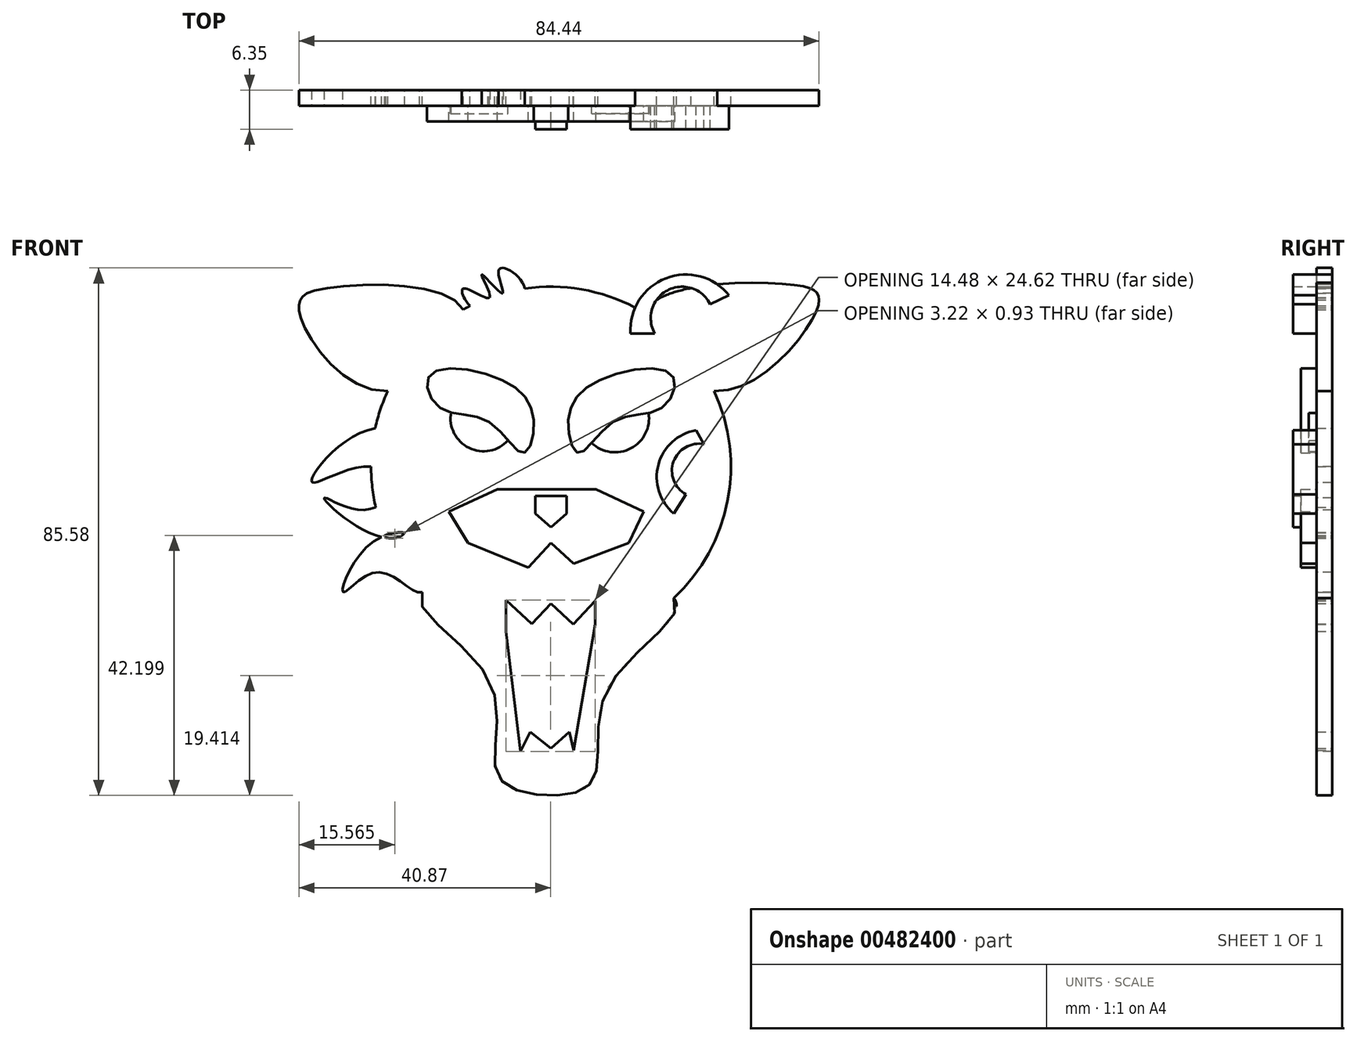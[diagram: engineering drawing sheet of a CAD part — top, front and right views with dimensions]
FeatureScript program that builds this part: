
annotation { "Feature Type Name" : "Feature", "Feature Type Description" : "" }
export const myFeature = defineFeature(function(context is Context, id is Id, definition is map)
    precondition{}
    {
        {
            var Q0;
            Q0=qCreatedBy(makeId("Front.planeOp"),FACE);
            var sketch = newSketch(context, id + "F0", { "sketchPlane" : qUnion([Q0])});
            skCircle(sketch, "E0", {"center": v(0, 0) * mm, "radius": 29.2 * mm});
            skFitSpline(sketch, "E1", {"points": [v(-20.92, -20.37) * mm, v(-10.1, -34.53) * mm, v(-8.7, -49.97) * mm, v(0, -53.34) * mm, v(7.02, -50.53) * mm, v(9.55, -35.37) * mm, v(19.93, -21.34) * mm, v(-20.92, -20.37) * mm]});
            skFitSpline(sketch, "E2", {"points": [v(-26.5, 12.27) * mm, v(-40.43, 23.58) * mm, v(-40.7, 26.95) * mm, v(-38.18, 28.64) * mm, v(-14.22, 25.5) * mm, v(-26.5, 12.27) * mm]});
            skFitSpline(sketch, "E3", {"points": [v(26.5, 12.27) * mm, v(42.95, 24.99) * mm, v(43.23, 28.07) * mm, v(39.58, 29.48) * mm, v(15.1, 25) * mm, v(26.5, 12.27) * mm]});
            skFitSpline(sketch, "E4", {"points": [v(-20.92, -20.37) * mm, v(-28.07, -17.12) * mm, v(-33.69, -20.37) * mm, v(-29.76, -12.91) * mm, v(-20.92, -12.35) * mm, v(-20.92, -20.37) * mm]});
            skFitSpline(sketch, "E5", {"points": [v(-23.75, -10.72) * mm, v(-31.72, -9.55) * mm, v(-36.78, -5.05) * mm, v(-30.6, -7.02) * mm, v(-24.14, -5.61) * mm, v(-23.75, -10.72) * mm]});
            skFitSpline(sketch, "E6", {"points": [v(-20.92, -3.09) * mm, v(-29.2, 0) * mm, v(-38.74, -2.53) * mm, v(-32.28, 4.77) * mm, v(-20.92, 4.21) * mm, v(-20.92, -3.09) * mm]});
            skFitSpline(sketch, "E7", {"points": [v(-10.67, 24.42) * mm, v(-14.22, 28.92) * mm, v(-9.96, 27.45) * mm, v(-11.23, 31.16) * mm, v(-7.86, 28.12) * mm, v(-8.42, 32) * mm, v(-4.24, 28.89) * mm, v(-10.67, 24.42) * mm]});
            skSolve(sketch);
        }
        {
            var Q0;
            Q0 = qSketchRegion(id + "F0", true);
            extrude(context, id + "F1", {"entities" : qUnion([Q0]), "depth" : 2.54 * mm});
        }
        {
            var Q0;
            Q0=qCreatedBy(makeId("Front.planeOp"),FACE);
            var sketch = newSketch(context, id + "F2", { "sketchPlane" : qUnion([Q0])});
            skFitSpline(sketch, "E8", {"points": [v(-17.97, 9.55) * mm, v(-10.1, 7.3) * mm, v(-4.5, 2.25) * mm, v(-2.8, 7.58) * mm, v(-7.86, 14.04) * mm, v(-19.65, 14.88) * mm, v(-17.97, 9.55) * mm]});
            skLineSegment(sketch, "E9", {"start": v(-8.7, -3.65) * mm, "end": v(0, -3.65) * mm});
            skLineSegment(sketch, "E10", {"start": v(0, -3.65) * mm, "end": v(7.3, -3.65) * mm});
            skLineSegment(sketch, "E11", {"start": v(7.3, -3.65) * mm, "end": v(15.02, -7.3) * mm});
            skLineSegment(sketch, "E12", {"start": v(15.02, -7.3) * mm, "end": v(12.63, -12.35) * mm});
            skLineSegment(sketch, "E13", {"start": v(12.63, -12.35) * mm, "end": v(3.65, -15.72) * mm});
            skLineSegment(sketch, "E14", {"start": v(3.65, -15.72) * mm, "end": v(0, -12.35) * mm});
            skLineSegment(sketch, "E15", {"start": v(0, -12.35) * mm, "end": v(-3.68, -16.34) * mm});
            skLineSegment(sketch, "E16", {"start": v(-3.68, -16.34) * mm, "end": v(-13.48, -12.35) * mm});
            skLineSegment(sketch, "E17", {"start": v(-13.48, -12.35) * mm, "end": v(-16.56, -7.3) * mm});
            skLineSegment(sketch, "E18", {"start": v(-16.56, -7.3) * mm, "end": v(-8.7, -3.65) * mm});
            skFitSpline(sketch, "E19.MirrorC", {"points": [v(17.97, 9.55) * mm, v(10.1, 7.3) * mm, v(4.5, 2.25) * mm, v(2.8, 7.58) * mm, v(7.86, 14.04) * mm, v(19.65, 14.88) * mm, v(17.97, 9.55) * mm]});
            skSolve(sketch);
        }
        {
            var Q0;
            Q0 = qSketchRegion(id + "F2", true);
            extrude(context, id + "F3", {"entities" : qUnion([Q0]), "operationType" : NewBodyOperationType.ADD, "depth" : 5.08 * mm});
        }
        {
            var Q0;
            Q0=qCreatedBy(makeId("Front.planeOp"),FACE);
            var sketch = newSketch(context, id + "F4", { "sketchPlane" : qUnion([Q0])});
            skLineSegment(sketch, "E20", {"start": v(-7.3, -26.7) * mm, "end": v(-7.3, -21.62) * mm});
            skLineSegment(sketch, "E21", {"start": v(-7.3, -21.62) * mm, "end": v(-3.09, -25.55) * mm});
            skLineSegment(sketch, "E22", {"start": v(-3.09, -25.55) * mm, "end": v(0, -22.24) * mm});
            skLineSegment(sketch, "E23", {"start": v(0, -22.24) * mm, "end": v(3.6, -25.6) * mm});
            skLineSegment(sketch, "E24", {"start": v(3.6, -25.6) * mm, "end": v(7.18, -21.77) * mm});
            skLineSegment(sketch, "E25", {"start": v(7.18, -21.77) * mm, "end": v(7.18, -25.6) * mm});
            skLineSegment(sketch, "E26", {"start": v(7.18, -25.6) * mm, "end": v(3.6, -46.6) * mm});
            skLineSegment(sketch, "E27", {"start": v(-4.93, -46.6) * mm, "end": v(-7.3, -26.7) * mm});
            skLineSegment(sketch, "E28", {"start": v(3.6, -46.6) * mm, "end": v(-4.93, -46.6) * mm});
            skSolve(sketch);
        }
        {
            var Q0;
            Q0 = qSketchRegion(id + "F4", true);
            extrude(context, id + "F5", {"entities" : qUnion([Q0]), "operationType" : NewBodyOperationType.REMOVE, "oppositeDirection" : true, "depth" : -2.54 * mm});
        }
        {
            var Q0;
            Q0=qCreatedBy(makeId("Front.planeOp"),FACE);
            var sketch = newSketch(context, id + "F6", { "sketchPlane" : qUnion([Q0])});
            skCircle(sketch, "E29", {"center": v(-10.95, 7.86) * mm, "radius": 5.36 * mm});
            skCircle(sketch, "E30", {"center": v(10.39, 7.86) * mm, "radius": 5.53 * mm});
            skSolve(sketch);
        }
        {
            var Q0;
            Q0 = qSketchRegion(id + "F6", true);
            extrude(context, id + "F7", {"entities" : qUnion([Q0]), "operationType" : NewBodyOperationType.ADD, "depth" : 3.8 * mm});
        }
        {
            var Q0;
            Q0=qCreatedBy(makeId("Front.planeOp"),FACE);
            var sketch = newSketch(context, id + "F8", { "sketchPlane" : qUnion([Q0])});
            skLineSegment(sketch, "E31", {"start": v(0, -9.83) * mm, "end": v(-2.53, -7.58) * mm});
            skLineSegment(sketch, "E32", {"start": v(-2.53, -7.58) * mm, "end": v(-2.53, -4.77) * mm});
            skLineSegment(sketch, "E33", {"start": v(-2.53, -4.77) * mm, "end": v(2.53, -4.77) * mm});
            skLineSegment(sketch, "E34", {"start": v(2.53, -4.77) * mm, "end": v(2.53, -7.58) * mm});
            skLineSegment(sketch, "E35", {"start": v(2.53, -7.58) * mm, "end": v(0, -9.83) * mm});
            skSolve(sketch);
        }
        {
            var Q0;
            Q0 = qSketchRegion(id + "F8", true);
            extrude(context, id + "F9", {"entities" : qUnion([Q0]), "operationType" : NewBodyOperationType.ADD, "depth" : 6.35 * mm});
        }
        {
            var Q0;
            Q0=qCreatedBy(makeId("Front.planeOp"),FACE);
            var sketch = newSketch(context, id + "F10", { "sketchPlane" : qUnion([Q0])});
            skArc(sketch, "E36", {"start": v(23.58, 5.9) * mm, "mid": v(17.43, 0.33) * mm, "end": v(19.93, -7.58) * mm});
            skArc(sketch, "E37", {"start": v(24.83, 3.65) * mm, "mid": v(19.9, 0.83) * mm, "end": v(21.9, -4.5) * mm});
            skArc(sketch, "E38", {"start": v(28.92, 27.8) * mm, "mid": v(18.65, 30.58) * mm, "end": v(12.91, 21.62) * mm});
            skArc(sketch, "E39", {"start": v(25.83, 26.39) * mm, "mid": v(18.9, 28.6) * mm, "end": v(16.84, 21.62) * mm});
            skLineSegment(sketch, "E40", {"start": v(12.91, 21.62) * mm, "end": v(16.84, 21.62) * mm});
            skLineSegment(sketch, "E41", {"start": v(25.83, 26.39) * mm, "end": v(28.92, 27.8) * mm});
            skLineSegment(sketch, "E42", {"start": v(24.83, 3.65) * mm, "end": v(23.58, 5.9) * mm});
            skLineSegment(sketch, "E43", {"start": v(19.93, -7.58) * mm, "end": v(21.9, -4.5) * mm});
            skSolve(sketch);
        }
        {
            var Q0;
            Q0 = qSketchRegion(id + "F10", true);
            extrude(context, id + "F11", {"entities" : qUnion([Q0]), "operationType" : NewBodyOperationType.ADD, "depth" : 6.35 * mm});
        }
        {
            var Q0;
            Q0=qCreatedBy(makeId("Front.planeOp"),FACE);
            var sketch = newSketch(context, id + "F12", { "sketchPlane" : qUnion([Q0])});
            skLineSegment(sketch, "E44", {"start": v(4.07, -47.62) * mm, "end": v(2.99, -43.03) * mm});
            skLineSegment(sketch, "E45", {"start": v(2.99, -43.03) * mm, "end": v(0, -45.73) * mm});
            skLineSegment(sketch, "E46", {"start": v(-3.4, -43.06) * mm, "end": v(-5.84, -47.96) * mm});
            skLineSegment(sketch, "E47", {"start": v(-5.84, -47.96) * mm, "end": v(4.07, -47.62) * mm});
            skLineSegment(sketch, "E48", {"start": v(0, -45.73) * mm, "end": v(-3.4, -43.06) * mm});
            skSolve(sketch);
        }
        {
            var Q0;
            Q0 = qSketchRegion(id + "F12", true);
            extrude(context, id + "F13", {"entities" : qUnion([Q0]), "operationType" : NewBodyOperationType.ADD, "depth" : 2.54 * mm});
        }
    });
